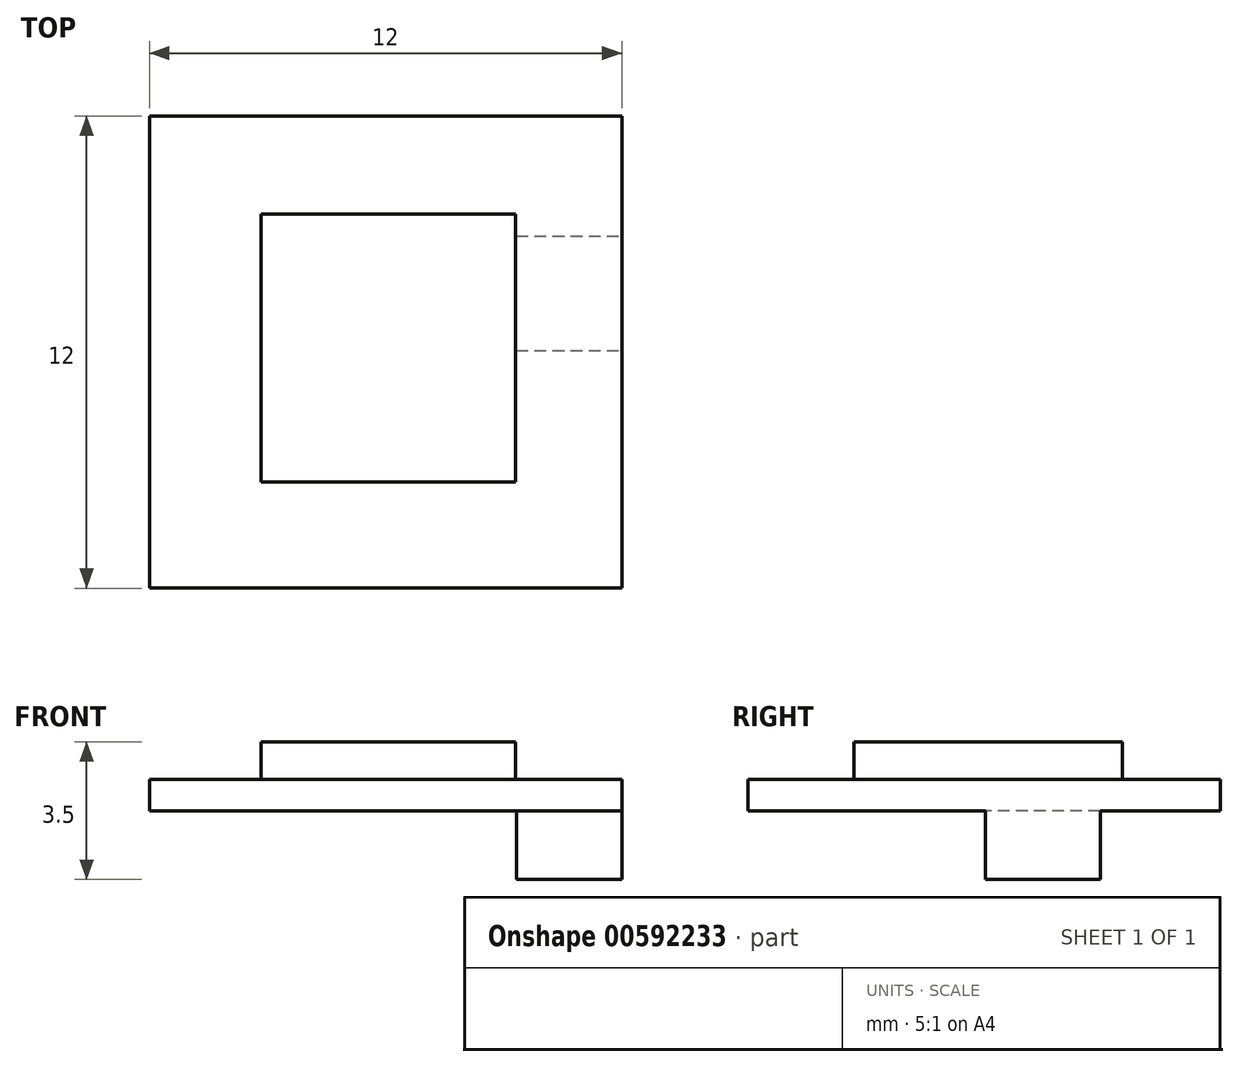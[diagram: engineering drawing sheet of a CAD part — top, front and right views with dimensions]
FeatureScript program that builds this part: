
annotation { "Feature Type Name" : "Feature", "Feature Type Description" : "" }
export const myFeature = defineFeature(function(context is Context, id is Id, definition is map)
    precondition{}
    {
        {
            var Q0;
            Q0=qCreatedBy(makeId("Top.planeOp"),FACE);
            var sketch = newSketch(context, id + "F0", { "sketchPlane" : qUnion([Q0])});
            skLineSegment(sketch, "E0.bottom", {"start": v(-6.12, 5.96) * mm, "end": v(5.88, 5.96) * mm});
            skLineSegment(sketch, "E0.top", {"start": v(-6.12, -6.04) * mm, "end": v(5.88, -6.04) * mm});
            skLineSegment(sketch, "E0.left", {"start": v(-6.12, 5.96) * mm, "end": v(-6.12, -6.04) * mm});
            skLineSegment(sketch, "E0.right", {"start": v(5.88, 5.96) * mm, "end": v(5.88, -6.04) * mm});
            skLineSegment(sketch, "E1.bottom", {"start": v(-3.28, 3.47) * mm, "end": v(3.18, 3.47) * mm});
            skLineSegment(sketch, "E1.top", {"start": v(-3.28, -3.34) * mm, "end": v(3.18, -3.34) * mm});
            skLineSegment(sketch, "E1.left", {"start": v(-3.28, 3.47) * mm, "end": v(-3.28, -3.34) * mm});
            skLineSegment(sketch, "E1.right", {"start": v(3.18, 3.47) * mm, "end": v(3.18, -3.34) * mm});
            skLineSegment(sketch, "E2.bottom", {"start": v(3.2, 2.91) * mm, "end": v(5.88, 2.91) * mm});
            skLineSegment(sketch, "E2.top", {"start": v(3.2, 0) * mm, "end": v(5.88, 0) * mm});
            skLineSegment(sketch, "E2.left", {"start": v(3.2, 2.91) * mm, "end": v(3.2, 0) * mm});
            skLineSegment(sketch, "E2.right", {"start": v(5.88, 2.91) * mm, "end": v(5.88, 0) * mm});
            skSolve(sketch);
        }
        {
            var Q0;
            {var subQ5=sQuery(id+"F0.wireOp",EDGE,"E0.bottom");Q0=makeQuery(id+"F0.imprint","IMPRINT",FACE,{"disambiguationData":[TD([[makeQuery(id+"F0.imprint","IMPRINT",EDGE,{"derivedFrom":subQ5}),-1.0]])]});}
            var Q1;
            Q1=makeQuery(id+"F0.imprint","IMPRINT",FACE,{"disambiguationData":[TD([[makeQuery(id+"F0.imprint","IMPRINT",EDGE,{"derivedFrom":sQuery(id+"F0.wireOp",EDGE,"E2.bottom")}),-1.0]])]});
            var Q2;
            Q2=makeQuery(id+"F0.imprint","IMPRINT",FACE,{"disambiguationData":[TD([[makeQuery(id+"F0.imprint","IMPRINT",EDGE,{"derivedFrom":sQuery(id+"F0.wireOp",EDGE,"E1.bottom")}),-1.0]])]});
            extrude(context, id + "F1", {"entities" : qUnion([Q0, Q1, Q2]), "depth" : 0.8 * mm, "offsetDistance" : 25 * mm});
        }
        {
            var Q0;
            Q0=makeQuery(id+"F0.imprint","IMPRINT",FACE,{"disambiguationData":[TD([[makeQuery(id+"F0.imprint","IMPRINT",EDGE,{"derivedFrom":sQuery(id+"F0.wireOp",EDGE,"E1.bottom")}),-1.0]])]});
            extrude(context, id + "F2", {"entities" : qUnion([Q0]), "operationType" : NewBodyOperationType.ADD, "depth" : 1.75 * mm, "offsetDistance" : 25 * mm});
        }
        {
            var Q0;
            Q0=makeQuery(id+"F0.imprint","IMPRINT",FACE,{"disambiguationData":[TD([[makeQuery(id+"F0.imprint","IMPRINT",EDGE,{"derivedFrom":sQuery(id+"F0.wireOp",EDGE,"E2.bottom")}),-1.0]])]});
            extrude(context, id + "F3", {"entities" : qUnion([Q0]), "operationType" : NewBodyOperationType.ADD, "oppositeDirection" : true, "depth" : 1.75 * mm, "offsetDistance" : 25 * mm});
        }
    });
